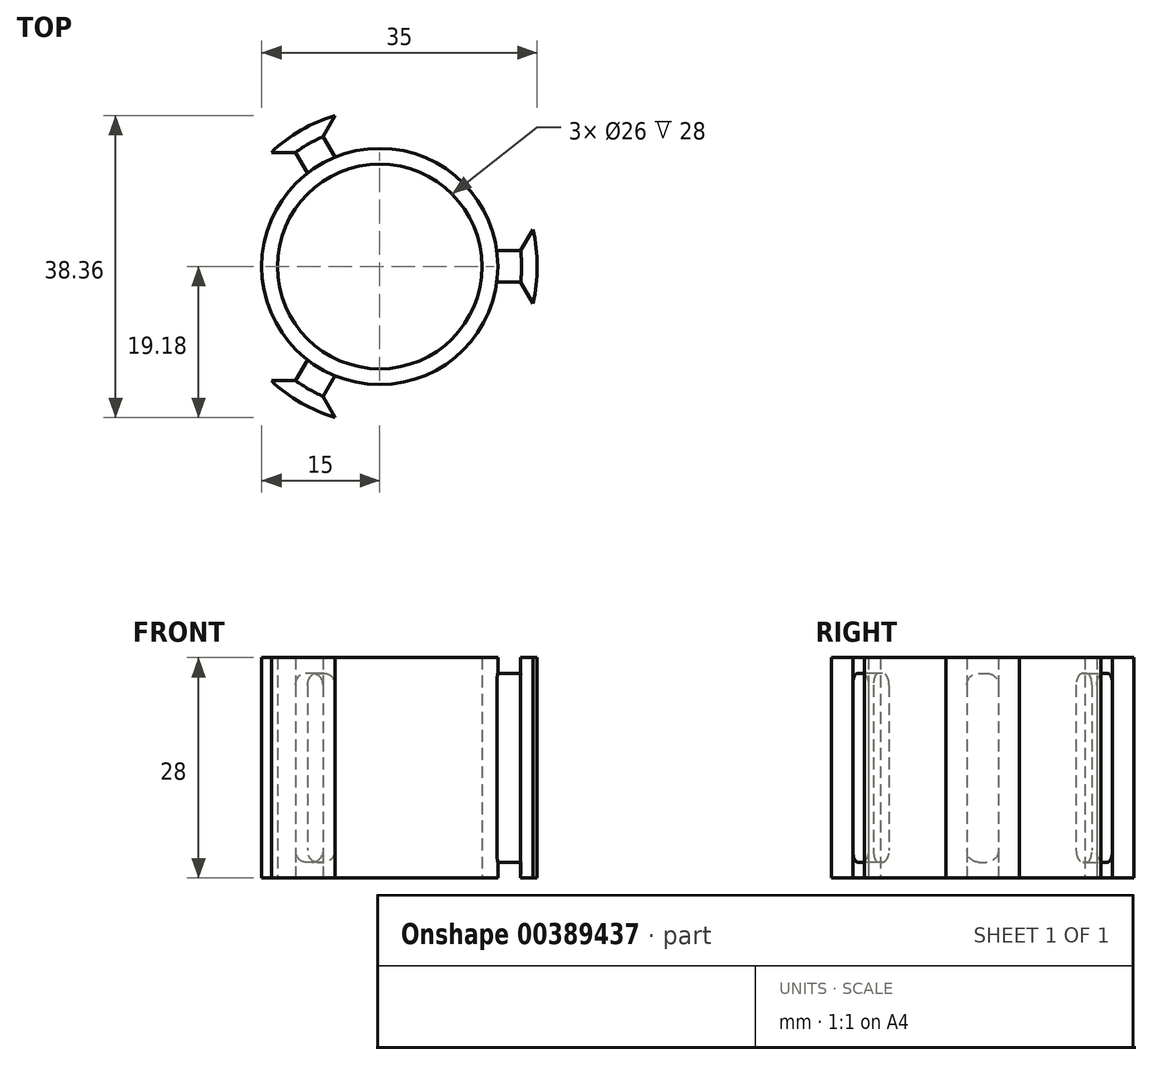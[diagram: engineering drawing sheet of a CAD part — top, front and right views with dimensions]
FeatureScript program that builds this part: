
annotation { "Feature Type Name" : "Feature", "Feature Type Description" : "" }
export const myFeature = defineFeature(function(context is Context, id is Id, definition is map)
    precondition{}
    {
        {
            var Q0;
            Q0=qCreatedBy(makeId("Top.planeOp"),FACE);
            var sketch = newSketch(context, id + "F0", { "sketchPlane" : qUnion([Q0])});
            skCircle(sketch, "E0", {"center": v(0, 0) * mm, "radius": 13 * mm});
            skCircle(sketch, "E1", {"center": v(0, 0) * mm, "radius": 15 * mm});
            skPoint(sketch, "E2.end.orphan", {"position": v(0, 21.28) * mm});
            skLineSegment(sketch, "E3", {"start": v(0, 0) * mm, "end": v(20, 0) * mm});
            skLineSegment(sketch, "E4", {"start": v(20, 0) * mm, "end": v(0, 0) * mm});
            skLineSegment(sketch, "E5", {"start": v(-10, -17.32) * mm, "end": v(0, 0) * mm});
            skLineSegment(sketch, "E6", {"start": v(0, 0) * mm, "end": v(-10, 17.32) * mm});
            skLineSegment(sketch, "E7", {"start": v(-9.17, 11.87) * mm, "end": v(-11.68, 16.23) * mm});
            skLineSegment(sketch, "E8", {"start": v(-5.7, 13.87) * mm, "end": v(-8.21, 18.22) * mm});
            skLineSegment(sketch, "E9", {"start": v(-11.73, 16.32) * mm, "end": v(-11.74, 16.31) * mm});
            skArc(sketch, "E10", {"start": v(-5.67, 19.18) * mm, "mid": v(-10, 17.32) * mm, "end": v(-13.77, 14.5) * mm});
            skLineSegment(sketch, "E11", {"start": v(-10.68, 14.5) * mm, "end": v(-13.77, 14.5) * mm});
            skLineSegment(sketch, "E12", {"start": v(-5.67, 19.18) * mm, "end": v(-7.22, 16.5) * mm});
            skPoint(sketch, "E13.orphan", {"position": v(-8.22, 18.23) * mm});
            skLineSegment(sketch, "E14.1.0", {"start": v(-9.17, -11.87) * mm, "end": v(-11.68, -16.22) * mm});
            skLineSegment(sketch, "E14.1.1", {"start": v(-13.77, -14.5) * mm, "end": v(-10.68, -14.5) * mm});
            skArc(sketch, "E14.1.2", {"start": v(-13.77, -14.5) * mm, "mid": v(-10, -17.32) * mm, "end": v(-5.67, -19.18) * mm});
            skLineSegment(sketch, "E14.1.3", {"start": v(-7.22, -16.5) * mm, "end": v(-5.67, -19.18) * mm});
            skLineSegment(sketch, "E14.1.4", {"start": v(-5.7, -13.87) * mm, "end": v(-8.22, -18.23) * mm});
            skLineSegment(sketch, "E14.2.0", {"start": v(14.87, -2) * mm, "end": v(19.89, -2) * mm});
            skLineSegment(sketch, "E14.2.1", {"start": v(19.45, -4.68) * mm, "end": v(17.9, -2) * mm});
            skArc(sketch, "E14.2.2", {"start": v(19.45, -4.68) * mm, "mid": v(20, 0) * mm, "end": v(19.45, 4.68) * mm});
            skLineSegment(sketch, "E14.2.3", {"start": v(17.9, 2) * mm, "end": v(19.45, 4.68) * mm});
            skLineSegment(sketch, "E14.2.4", {"start": v(14.87, 2) * mm, "end": v(19.9, 2) * mm});
            skSolve(sketch);
        }
        {
            var Q0;
            Q0=qSketchRegion(id+"F0",true);
            extrude(context, id + "F1", {"entities" : qUnion([Q0]), "depth" : 28 * mm});
        }
        {
            var Q0;
            Q0=qCreatedBy(makeId("Top.planeOp"),FACE);
            var sketch = newSketch(context, id + "F2", { "sketchPlane" : qUnion([Q0])});
            skCircle(sketch, "E15", {"center": v(0, 0) * mm, "radius": 15 * mm});
            skCircle(sketch, "E16", {"center": v(0, 0) * mm, "radius": 18 * mm});
            skSolve(sketch);
        }
        {
            var Q0;
            Q0=makeQuery(id+"F2.imprint","IMPRINT",FACE,{"disambiguationData":[TD([[makeQuery(id+"F2.imprint","IMPRINT",EDGE,{"derivedFrom":sQuery(id+"F2.wireOp",EDGE,"E15")}),-1.0]])]});
            extrude(context, id + "F3", {"entities" : qUnion([Q0]), "operationType" : NewBodyOperationType.REMOVE, "depth" : 2 * mm});
        }
        {
            var Q0;
            Q0=makeQuery(id+"F1.opExtrude","CAP_FACE",FACE,{"disambiguationData":[OSD([sQuery(id+"F0.wireOp",EDGE,"E0"),sQuery(id+"F0.wireOp",EDGE,"E1"),sQuery(id+"F0.wireOp",EDGE,"E7"),sQuery(id+"F0.wireOp",EDGE,"E8"),sQuery(id+"F0.wireOp",EDGE,"E10"),sQuery(id+"F0.wireOp",EDGE,"E11"),sQuery(id+"F0.wireOp",EDGE,"E12"),sQuery(id+"F0.wireOp",EDGE,"E14.1.0"),sQuery(id+"F0.wireOp",EDGE,"E14.1.1"),sQuery(id+"F0.wireOp",EDGE,"E14.1.2"),sQuery(id+"F0.wireOp",EDGE,"E14.1.3"),sQuery(id+"F0.wireOp",EDGE,"E14.1.4"),sQuery(id+"F0.wireOp",EDGE,"E14.2.0"),sQuery(id+"F0.wireOp",EDGE,"E14.2.1"),sQuery(id+"F0.wireOp",EDGE,"E14.2.2"),sQuery(id+"F0.wireOp",EDGE,"E14.2.3"),sQuery(id+"F0.wireOp",EDGE,"E14.2.4")])],"isStart":false});
            var sketch = newSketch(context, id + "F4", { "sketchPlane" : qUnion([Q0])});
            skCircle(sketch, "E17", {"center": v(0, 0) * mm, "radius": 15 * mm});
            skCircle(sketch, "E18", {"center": v(0, 0) * mm, "radius": 18.01 * mm});
            skSolve(sketch);
        }
        {
            var Q0;
            Q0=qSketchRegion(id+"F4",true);
            extrude(context, id + "F5", {"entities" : qUnion([Q0]), "operationType" : NewBodyOperationType.REMOVE, "oppositeDirection" : true, "depth" : 2 * mm});
        }
        {
            var Q0;
            Q0=makeQuery(id+"F5.boolean.opBoolean","INTERSECT",EDGE,{"derivedFrom":[makeQuery(id+"F1.opExtrude","SWEPT_FACE",FACE,{"disambiguationData":[OSD([sQuery(id+"F0.wireOp",EDGE,"E14.1.4")])]}),makeQuery(id+"F5.opExtrude","CAP_FACE",FACE,{"disambiguationData":[OSD([sQuery(id+"F4.wireOp",EDGE,"E17"),sQuery(id+"F4.wireOp",EDGE,"E18")])],"isStart":false})]});
            var Q1;
            Q1=makeQuery(id+"F5.boolean.opBoolean","INTERSECT",EDGE,{"derivedFrom":[makeQuery(id+"F1.opExtrude","SWEPT_FACE",FACE,{"disambiguationData":[OSD([sQuery(id+"F0.wireOp",EDGE,"E14.1.0")])]}),makeQuery(id+"F5.opExtrude","CAP_FACE",FACE,{"disambiguationData":[OSD([sQuery(id+"F4.wireOp",EDGE,"E17"),sQuery(id+"F4.wireOp",EDGE,"E18")])],"isStart":false})]});
            var Q2;
            Q2=makeQuery(id+"F5.boolean.opBoolean","INTERSECT",EDGE,{"derivedFrom":[makeQuery(id+"F1.opExtrude","SWEPT_FACE",FACE,{"disambiguationData":[OSD([sQuery(id+"F0.wireOp",EDGE,"E14.2.0")])]}),makeQuery(id+"F5.opExtrude","CAP_FACE",FACE,{"disambiguationData":[OSD([sQuery(id+"F4.wireOp",EDGE,"E17"),sQuery(id+"F4.wireOp",EDGE,"E18")])],"isStart":false})]});
            var Q3;
            Q3=makeQuery(id+"F5.boolean.opBoolean","INTERSECT",EDGE,{"derivedFrom":[makeQuery(id+"F1.opExtrude","SWEPT_FACE",FACE,{"disambiguationData":[OSD([sQuery(id+"F0.wireOp",EDGE,"E14.2.4")])]}),makeQuery(id+"F5.opExtrude","CAP_FACE",FACE,{"disambiguationData":[OSD([sQuery(id+"F4.wireOp",EDGE,"E17"),sQuery(id+"F4.wireOp",EDGE,"E18")])],"isStart":false})]});
            var Q4;
            Q4=makeQuery(id+"F5.boolean.opBoolean","INTERSECT",EDGE,{"derivedFrom":[makeQuery(id+"F1.opExtrude","SWEPT_FACE",FACE,{"disambiguationData":[OSD([sQuery(id+"F0.wireOp",EDGE,"E8")])]}),makeQuery(id+"F5.opExtrude","CAP_FACE",FACE,{"disambiguationData":[OSD([sQuery(id+"F4.wireOp",EDGE,"E17"),sQuery(id+"F4.wireOp",EDGE,"E18")])],"isStart":false})]});
            var Q5;
            Q5=makeQuery(id+"F5.boolean.opBoolean","INTERSECT",EDGE,{"derivedFrom":[makeQuery(id+"F1.opExtrude","SWEPT_FACE",FACE,{"disambiguationData":[OSD([sQuery(id+"F0.wireOp",EDGE,"E7")])]}),makeQuery(id+"F5.opExtrude","CAP_FACE",FACE,{"disambiguationData":[OSD([sQuery(id+"F4.wireOp",EDGE,"E17"),sQuery(id+"F4.wireOp",EDGE,"E18")])],"isStart":false})]});
            var Q6;
            Q6=makeQuery(id+"F3.boolean.opBoolean","INTERSECT",EDGE,{"derivedFrom":[makeQuery(id+"F1.opExtrude","SWEPT_FACE",FACE,{"disambiguationData":[OSD([sQuery(id+"F0.wireOp",EDGE,"E7")])]}),makeQuery(id+"F3.opExtrude","CAP_FACE",FACE,{"disambiguationData":[OSD([sQuery(id+"F2.wireOp",EDGE,"E15"),sQuery(id+"F2.wireOp",EDGE,"E16")])],"isStart":false})]});
            var Q7;
            Q7=makeQuery(id+"F3.boolean.opBoolean","INTERSECT",EDGE,{"derivedFrom":[makeQuery(id+"F1.opExtrude","SWEPT_FACE",FACE,{"disambiguationData":[OSD([sQuery(id+"F0.wireOp",EDGE,"E8")])]}),makeQuery(id+"F3.opExtrude","CAP_FACE",FACE,{"disambiguationData":[OSD([sQuery(id+"F2.wireOp",EDGE,"E15"),sQuery(id+"F2.wireOp",EDGE,"E16")])],"isStart":false})]});
            var Q8;
            Q8=makeQuery(id+"F3.boolean.opBoolean","INTERSECT",EDGE,{"derivedFrom":[makeQuery(id+"F1.opExtrude","SWEPT_FACE",FACE,{"disambiguationData":[OSD([sQuery(id+"F0.wireOp",EDGE,"E14.2.4")])]}),makeQuery(id+"F3.opExtrude","CAP_FACE",FACE,{"disambiguationData":[OSD([sQuery(id+"F2.wireOp",EDGE,"E15"),sQuery(id+"F2.wireOp",EDGE,"E16")])],"isStart":false})]});
            var Q9;
            Q9=makeQuery(id+"F3.boolean.opBoolean","INTERSECT",EDGE,{"derivedFrom":[makeQuery(id+"F1.opExtrude","SWEPT_FACE",FACE,{"disambiguationData":[OSD([sQuery(id+"F0.wireOp",EDGE,"E14.2.0")])]}),makeQuery(id+"F3.opExtrude","CAP_FACE",FACE,{"disambiguationData":[OSD([sQuery(id+"F2.wireOp",EDGE,"E15"),sQuery(id+"F2.wireOp",EDGE,"E16")])],"isStart":false})]});
            var Q10;
            Q10=makeQuery(id+"F3.boolean.opBoolean","INTERSECT",EDGE,{"derivedFrom":[makeQuery(id+"F1.opExtrude","SWEPT_FACE",FACE,{"disambiguationData":[OSD([sQuery(id+"F0.wireOp",EDGE,"E14.1.0")])]}),makeQuery(id+"F3.opExtrude","CAP_FACE",FACE,{"disambiguationData":[OSD([sQuery(id+"F2.wireOp",EDGE,"E15"),sQuery(id+"F2.wireOp",EDGE,"E16")])],"isStart":false})]});
            var Q11;
            Q11=makeQuery(id+"F3.boolean.opBoolean","INTERSECT",EDGE,{"derivedFrom":[makeQuery(id+"F1.opExtrude","SWEPT_FACE",FACE,{"disambiguationData":[OSD([sQuery(id+"F0.wireOp",EDGE,"E14.1.4")])]}),makeQuery(id+"F3.opExtrude","CAP_FACE",FACE,{"disambiguationData":[OSD([sQuery(id+"F2.wireOp",EDGE,"E15"),sQuery(id+"F2.wireOp",EDGE,"E16")])],"isStart":false})]});
            fillet(context, id + "F6", {"entities" : qUnion([Q0, Q1, Q2, Q3, Q4, Q5, Q6, Q7, Q8, Q9, Q10, Q11]), "radius" : 1.5 * mm, "tangentPropagation" : true, "allowEdgeOverflow" : false});
        }
    });
